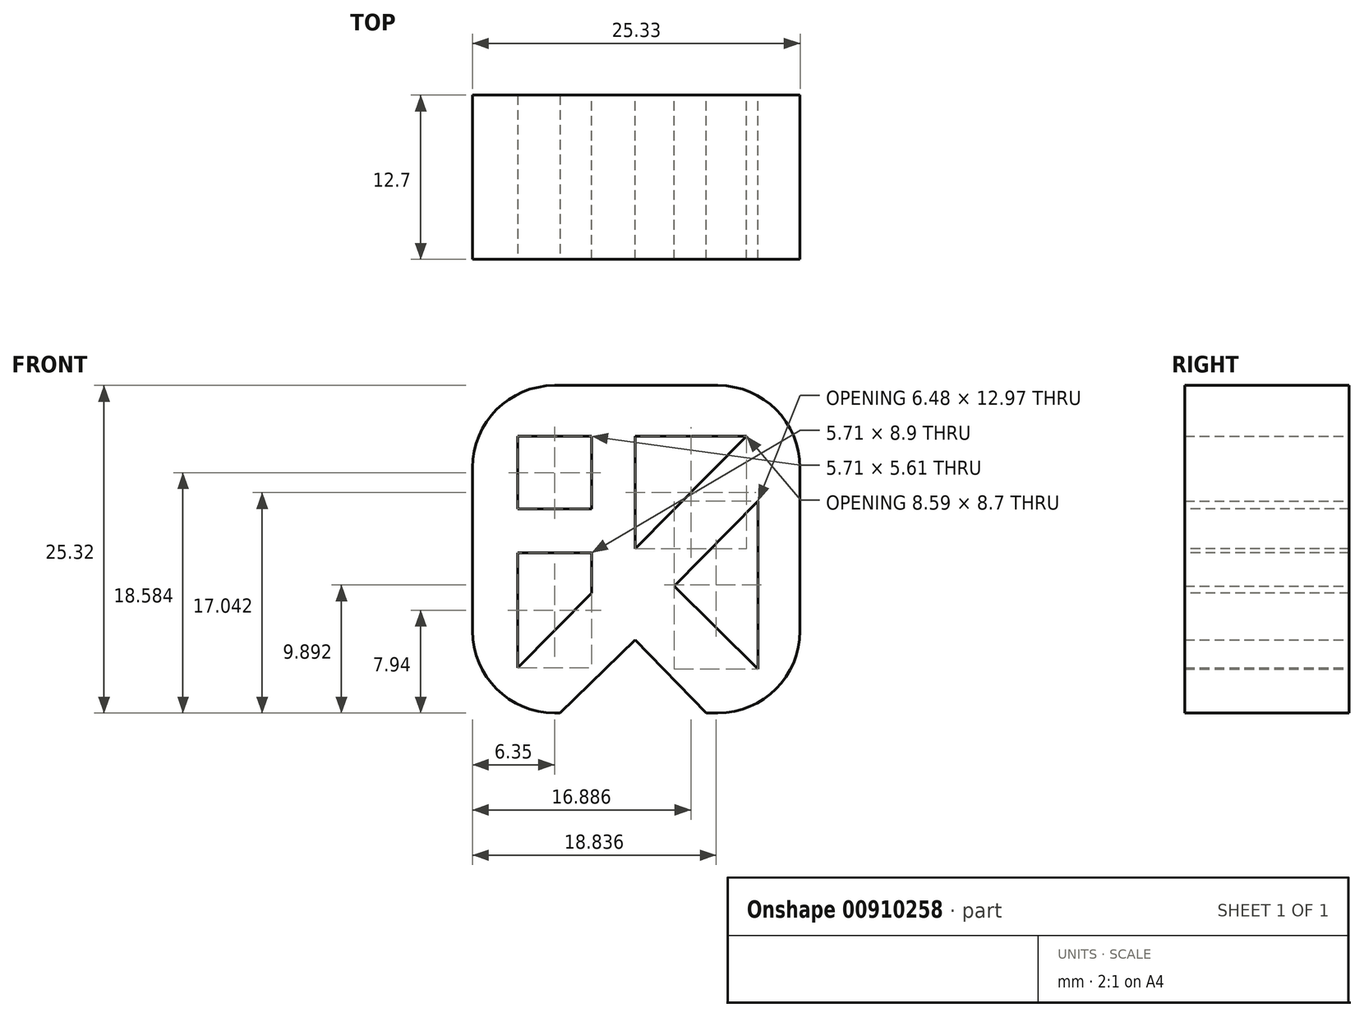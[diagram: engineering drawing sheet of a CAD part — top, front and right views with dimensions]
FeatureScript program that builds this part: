
annotation { "Feature Type Name" : "Feature", "Feature Type Description" : "" }
export const myFeature = defineFeature(function(context is Context, id is Id, definition is map)
    precondition{}
    {
        {
            var Q0;
            Q0=qCreatedBy(makeId("Front.planeOp"),FACE);
            var sketch = newSketch(context, id + "F0", { "sketchPlane" : qUnion([Q0])});
            skLineSegment(sketch, "E0.bottom", {"start": v(-47.03, 38.86) * mm, "end": v(-34.4, 38.86) * mm});
            skLineSegment(sketch, "E0.top", {"start": v(-47.03, 13.54) * mm, "end": v(-34.4, 13.54) * mm});
            skLineSegment(sketch, "E0.left", {"start": v(-53.38, 32.5) * mm, "end": v(-53.38, 19.89) * mm});
            skLineSegment(sketch, "E0.right", {"start": v(-28.05, 32.5) * mm, "end": v(-28.05, 19.89) * mm});
            skPoint(sketch, "E1.visualSharp", {"position": v(-28.05, 38.86) * mm});
            skArc(sketch, "E1.filletArc", {"start": v(-28.05, 32.5) * mm, "mid": v(-29.91, 37) * mm, "end": v(-34.4, 38.86) * mm});
            skPoint(sketch, "E2.visualSharp", {"position": v(-53.38, 38.86) * mm});
            skArc(sketch, "E2.filletArc", {"start": v(-47.03, 38.86) * mm, "mid": v(-51.52, 37) * mm, "end": v(-53.38, 32.5) * mm});
            skPoint(sketch, "E3.visualSharp", {"position": v(-28.05, 13.54) * mm});
            skArc(sketch, "E3.filletArc", {"start": v(-34.4, 13.54) * mm, "mid": v(-29.91, 15.4) * mm, "end": v(-28.05, 19.89) * mm});
            skPoint(sketch, "E4.visualSharp", {"position": v(-53.38, 13.54) * mm});
            skArc(sketch, "E4.filletArc", {"start": v(-53.38, 19.89) * mm, "mid": v(-51.52, 15.4) * mm, "end": v(-47.03, 13.54) * mm});
            skSolve(sketch);
        }
        {
            var Q0;
            Q0=qCreatedBy(makeId("Front.planeOp"),FACE);
            var sketch = newSketch(context, id + "F1", { "sketchPlane" : qUnion([Q0])});
            skLineSegment(sketch, "E5", {"start": v(-49.88, 34.93) * mm, "end": v(-49.88, 17.03) * mm});
            skLineSegment(sketch, "E6", {"start": v(-49.88, 17.03) * mm, "end": v(-32.2, 34.93) * mm});
            skLineSegment(sketch, "E7", {"start": v(-32.2, 34.93) * mm, "end": v(-49.88, 34.93) * mm});
            skLineSegment(sketch, "E8", {"start": v(-31.3, 29.92) * mm, "end": v(-37.79, 23.35) * mm});
            skLineSegment(sketch, "E9", {"start": v(-37.79, 23.35) * mm, "end": v(-31.3, 16.95) * mm});
            skLineSegment(sketch, "E10", {"start": v(-31.3, 16.95) * mm, "end": v(-31.3, 29.92) * mm});
            skSolve(sketch);
        }
        {
            var Q0;
            Q0 = qSketchRegion(id + "F0", true);
            extrude(context, id + "F2", {"entities" : qUnion([Q0]), "depth" : 12.7 * mm, "offsetDistance" : 25.4 * mm});
        }
        {
            var Q0;
            Q0 = qSketchRegion(id + "F1", true);
            extrude(context, id + "F3", {"entities" : qUnion([Q0]), "operationType" : NewBodyOperationType.REMOVE, "endBound" : BoundingType.SYMMETRIC, "depth" : 50.8 * mm, "offsetDistance" : 25.4 * mm});
        }
        {
            var Q0;
            Q0=qCreatedBy(makeId("Front.planeOp"),FACE);
            var sketch = newSketch(context, id + "F4", { "sketchPlane" : qUnion([Q0])});
            skLineSegment(sketch, "E11.bottom", {"start": v(-44.18, 21.92) * mm, "end": v(-40.79, 21.92) * mm});
            skLineSegment(sketch, "E11.top", {"start": v(-44.18, 36.71) * mm, "end": v(-40.79, 36.71) * mm});
            skLineSegment(sketch, "E11.left", {"start": v(-44.18, 21.92) * mm, "end": v(-44.18, 36.71) * mm});
            skLineSegment(sketch, "E11.right", {"start": v(-40.79, 21.92) * mm, "end": v(-40.79, 36.71) * mm});
            skLineSegment(sketch, "E12.bottom", {"start": v(-51.33, 25.93) * mm, "end": v(-44.18, 25.93) * mm});
            skLineSegment(sketch, "E12.top", {"start": v(-51.33, 29.32) * mm, "end": v(-44.18, 29.32) * mm});
            skLineSegment(sketch, "E12.left", {"start": v(-51.33, 25.93) * mm, "end": v(-51.33, 29.32) * mm});
            skLineSegment(sketch, "E12.right", {"start": v(-44.18, 25.93) * mm, "end": v(-44.18, 29.32) * mm});
            skSolve(sketch);
        }
        {
            var Q0;
            Q0 = qSketchRegion(id + "F4", true);
            extrude(context, id + "F5", {"entities" : qUnion([Q0]), "operationType" : NewBodyOperationType.ADD, "depth" : 12.7 * mm, "offsetDistance" : 25.4 * mm});
        }
        {
            var Q0;
            Q0=makeQuery(id+"F5.boolean.opBoolean","MERGE",FACE,{"derivedFrom":[makeQuery(id+"F2.opExtrude","CAP_FACE",FACE,{"disambiguationData":[OSD([sQuery(id+"F0.wireOp",EDGE,"E0.bottom"),sQuery(id+"F0.wireOp",EDGE,"E0.top"),sQuery(id+"F0.wireOp",EDGE,"E0.left"),sQuery(id+"F0.wireOp",EDGE,"E0.right"),sQuery(id+"F0.wireOp",EDGE,"E1.filletArc"),sQuery(id+"F0.wireOp",EDGE,"E2.filletArc"),sQuery(id+"F0.wireOp",EDGE,"E3.filletArc"),sQuery(id+"F0.wireOp",EDGE,"E4.filletArc")])],"isStart":true}),makeQuery(id+"F5.opExtrude","CAP_FACE",FACE,{"disambiguationData":[OSD([sQuery(id+"F4.wireOp",EDGE,"E11.bottom"),sQuery(id+"F4.wireOp",EDGE,"E11.top"),sQuery(id+"F4.wireOp",EDGE,"E11.left"),sQuery(id+"F4.wireOp",EDGE,"E11.right"),sQuery(id+"F4.wireOp",EDGE,"E12.bottom"),sQuery(id+"F4.wireOp",EDGE,"E12.top"),sQuery(id+"F4.wireOp",EDGE,"E12.left")])],"isStart":true})]});
            var sketch = newSketch(context, id + "F6", { "sketchPlane" : qUnion([Q0])});
            skLineSegment(sketch, "E13", {"start": v(47.08, 13.07) * mm, "end": v(40.79, 19.18) * mm});
            skLineSegment(sketch, "E14", {"start": v(40.79, 19.18) * mm, "end": v(33.4, 11.57) * mm});
            skLineSegment(sketch, "E15", {"start": v(47.08, 13.07) * mm, "end": v(33.4, 11.57) * mm});
            skSolve(sketch);
        }
        {
            var Q0;
            {var subQ0=sQuery(id+"F6.wireOp",EDGE,"E14");var subQ1=sQuery(id+"F6.wireOp",EDGE,"E13");var subQ2=makeQuery(id+"F6.imprint","INTERSECT",VERTEX,{"derivedFrom":[subQ1,subQ0]});Q0=makeQuery(id+"F6.imprint","IMPRINT",FACE,{"disambiguationData":[TD([[makeQuery(id+"F6.imprint","IMPRINT",EDGE,{"disambiguationData":[TD([[subQ2,1.0]])],"derivedFrom":subQ1}),1.0]])]});}
            var Q1;
            {var subQ0=sQuery(id+"F6.wireOp",EDGE,"E15");Q1=makeQuery(id+"F6.imprint","IMPRINT",FACE,{"disambiguationData":[TD([[makeQuery(id+"F6.imprint","IMPRINT",EDGE,{"derivedFrom":subQ0}),-1.0]])]});}
            extrude(context, id + "F7", {"entities" : qUnion([Q0, Q1]), "operationType" : NewBodyOperationType.REMOVE, "oppositeDirection" : true, "depth" : 254 * mm, "offsetDistance" : 25.4 * mm});
        }
    });
